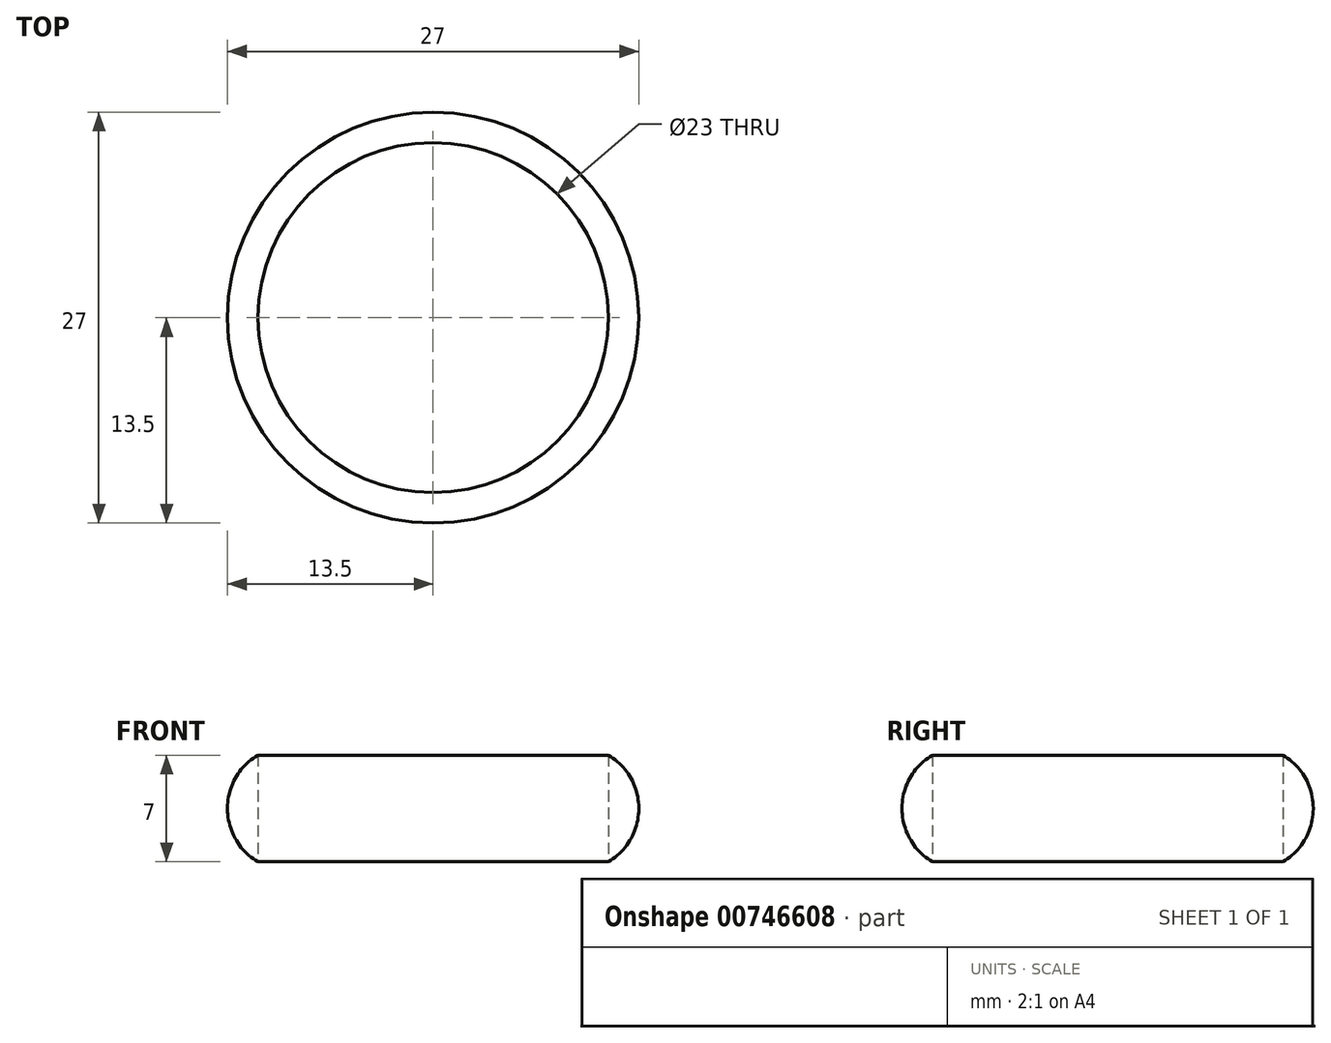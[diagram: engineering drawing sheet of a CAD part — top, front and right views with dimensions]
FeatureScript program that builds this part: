
annotation { "Feature Type Name" : "Feature", "Feature Type Description" : "" }
export const myFeature = defineFeature(function(context is Context, id is Id, definition is map)
    precondition{}
    {
        {
            var Q0;
            Q0=qCreatedBy(makeId("Top.planeOp"),FACE);
            var sketch = newSketch(context, id + "F0", { "sketchPlane" : qUnion([Q0])});
            skCircle(sketch, "E0", {"center": v(0, 0) * mm, "radius": 13.5 * mm});
            skCircle(sketch, "E1", {"center": v(0, 0) * mm, "radius": 11.5 * mm});
            skText(sketch, "E2", { "text": "dsds", "fontName": "OpenSans-Regular.ttf"});
            const initialGuessF0  = {"E2": [-0.00929, -0.00443, 1, 0, 0.01122]};
            skSetInitialGuess(sketch, initialGuessF0);
            skSolve(sketch);
        }
        {
            var Q0;
            Q0=makeQuery(id+"F0.imprint","IMPRINT",FACE,{"disambiguationData":[TD([[makeQuery(id+"F0.imprint","IMPRINT",EDGE,{"derivedFrom":sQuery(id+"F0.wireOp",EDGE,"E0")}),1.0]])]});
            extrude(context, id + "F1", {"entities" : qUnion([Q0]), "depth" : 7 * mm, "offsetDistance" : 25 * mm});
        }
        {
            var Q0;
            Q0=makeQuery(id+"F1.opExtrude","CAP_EDGE",EDGE,{"disambiguationData":[OSD([sQuery(id+"F0.wireOp",EDGE,"E0")])],"isStart":false});
            fillet(context, id + "F2", {"entities" : qUnion([Q0]), "radius" : 4 * mm, "tangentPropagation" : true, "allowEdgeOverflow" : false});
        }
        {
            var Q0;
            Q0=makeQuery(id+"F1.opExtrude","CAP_EDGE",EDGE,{"disambiguationData":[OSD([sQuery(id+"F0.wireOp",EDGE,"E0")])],"isStart":true});
            fillet(context, id + "F3", {"entities" : qUnion([Q0]), "radius" : 4 * mm, "tangentPropagation" : true, "allowEdgeOverflow" : false});
        }
    });
